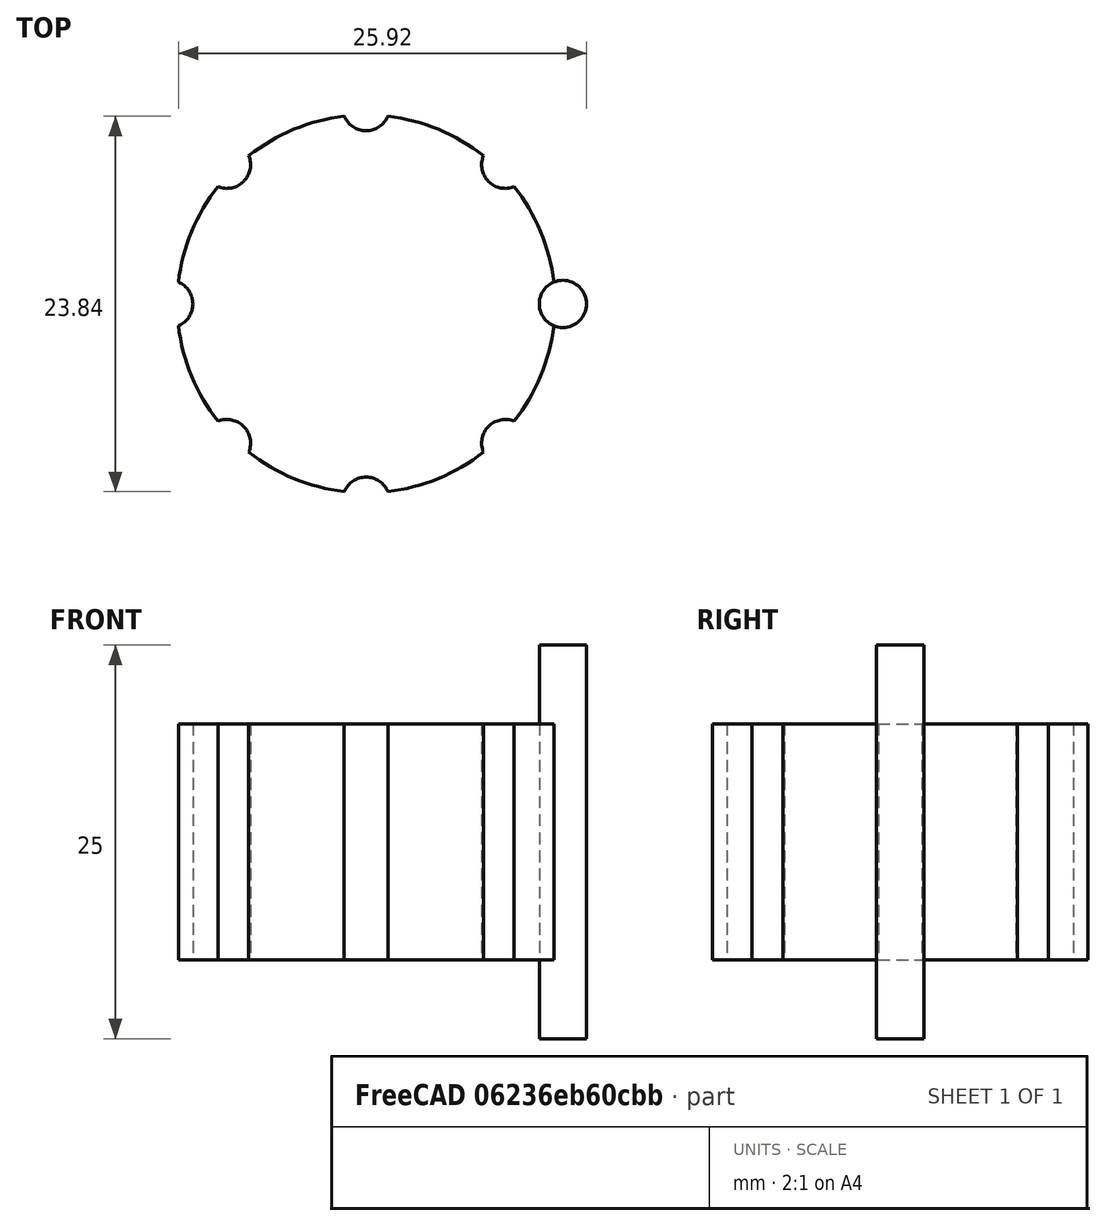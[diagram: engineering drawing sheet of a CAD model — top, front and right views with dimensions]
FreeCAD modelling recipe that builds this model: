
FCSTD DOCUMENT  (FreeCAD 0.21R33771 (Git))
Label: OJT1_T11R01_boto seleccio
License: All rights reserved
LicenseURL: http://en.wikipedia.org/wiki/All_rights_reserved
objects: Part::Cylinder×2, Part::FeaturePython×1, Part::Cut×1
note: 3 computed .brp shape members not serialized (recipe doc carries the construction recipe); baked Part::Feature solids carry a one-line shape summary decoded from their .brp

FEATURE [Part::Cylinder] Cylinder
  Angle = 360
  AttacherType = Attacher::AttachEngine3D
  FirstAngle = 0
  Height = 15
  Radius = 12
  SecondAngle = 0
FEATURE [Part::Cylinder] Cylinder001
  Angle = 360
  AttacherType = Attacher::AttachEngine3D
  FirstAngle = 0
  Height = 25
  Placement = pos=(12.5,0,-5) rot=(0,0,1;0rad)
  Radius = 1.5
  SecondAngle = 0
FEATURE [Part::FeaturePython] Array  # Draft array (typed FeaturePython)
  AlwaysSyncPlacement = false
  Angle = 360
  ArrayType = 1
  Axis = (0,0,0)
  Base = -> Cylinder001
  Center = (0,0,0)
  Count = 8
  ExpandArray = false
  Fuse = false
  IntervalAxis = (0,0,0)
  IntervalX = (50,0,0)
  IntervalY = (0,50,0)
  IntervalZ = (0,0,50)
  NumberCircles = 3
  NumberPolar = 8
  NumberX = 2
  NumberY = 2
  NumberZ = 1
  PlacementList = 8 placements: [(12.5,0,-5),(8.83883,8.83883,-5),(2.77556e-15,12.5,-5),(-8.83883,8.83883,-5),(-12.5,1.53081e-15,-5),(-8.83883,-8.83883,-5),(-2.77556e-15,-12.5,-5),(8.83883,-8.83883,-5)]
  RadialDistance = 50
  ScaleList = (8) [(1,1,1),(1,1,1),(1,1,1),(1,1,1),(1,1,1),(1,1,1),(1,1,1),(1,1,1)]
  Symmetry = 1
  TangentialDistance = 25
FEATURE [Part::Cut] Cut  label="boto"
  Base = -> Cylinder
  Refine = true
  Tool = -> Array
